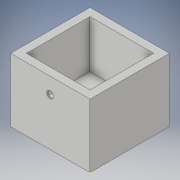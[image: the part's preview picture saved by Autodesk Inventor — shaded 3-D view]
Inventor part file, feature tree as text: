
AUTODESK INVENTOR PART (.ipt)
format: ipt  version: 2019 (Build 230136000, 136)  size: 140,288 bytes
history: native  units: in
note: dims shown in document units (in); Inventor stores cm internally (conversion verified against a paired STEP export)
features: sketch x6, extrude x5, chamfer x1
ambient origin geometry x8: Origin, YZ Plane, XZ Plane, XY Plane, X Axis, Y Axis, Z Axis, Center Point
bodies: Solid1 (feature_tree)
feature tree (12):
  extrude  "Extrusion1"  Depth=5.0in
  extrude  "Extrusion2"  Depth=4.0in
  sketch  "Sketch3"  dims[d5=4.0in d6=0.5in]
  extrude  "Extrusion3"  Depth=0.5in
  extrude  "Extrusion4"  Depth=3.0in
  chamfer  "Chamfer2"  Distance=3.0in
  extrude  "Extrusion5"  Depth=1.0in
  sketch  "Sketch1"  dims[d0=5.0in d1=5.0in]
  sketch  "Sketch2"  dims[d2=4.0in d3=0.0in d4=4.0in]
  sketch  "Sketch4"  dims[d7=0.5in d8=3.0in]
  sketch  "Sketch5"  dims[d9=0.0in]
  sketch  "Sketch6"  dims[d10=0.433in d11=3.0in d12=2.5in d13=3.0in d14=0.0in d15=1.4in d16=2.0in d17=2.0in d18=0.425in d19=0.0in d23=0.425in d24=0.125in d25=30.0deg d26=0.4884in d27=0.4884in d28=2.2558in d29=2.2558in d30=2.2558in d31=2.2558in d32=1.0in d33=0.0in]
